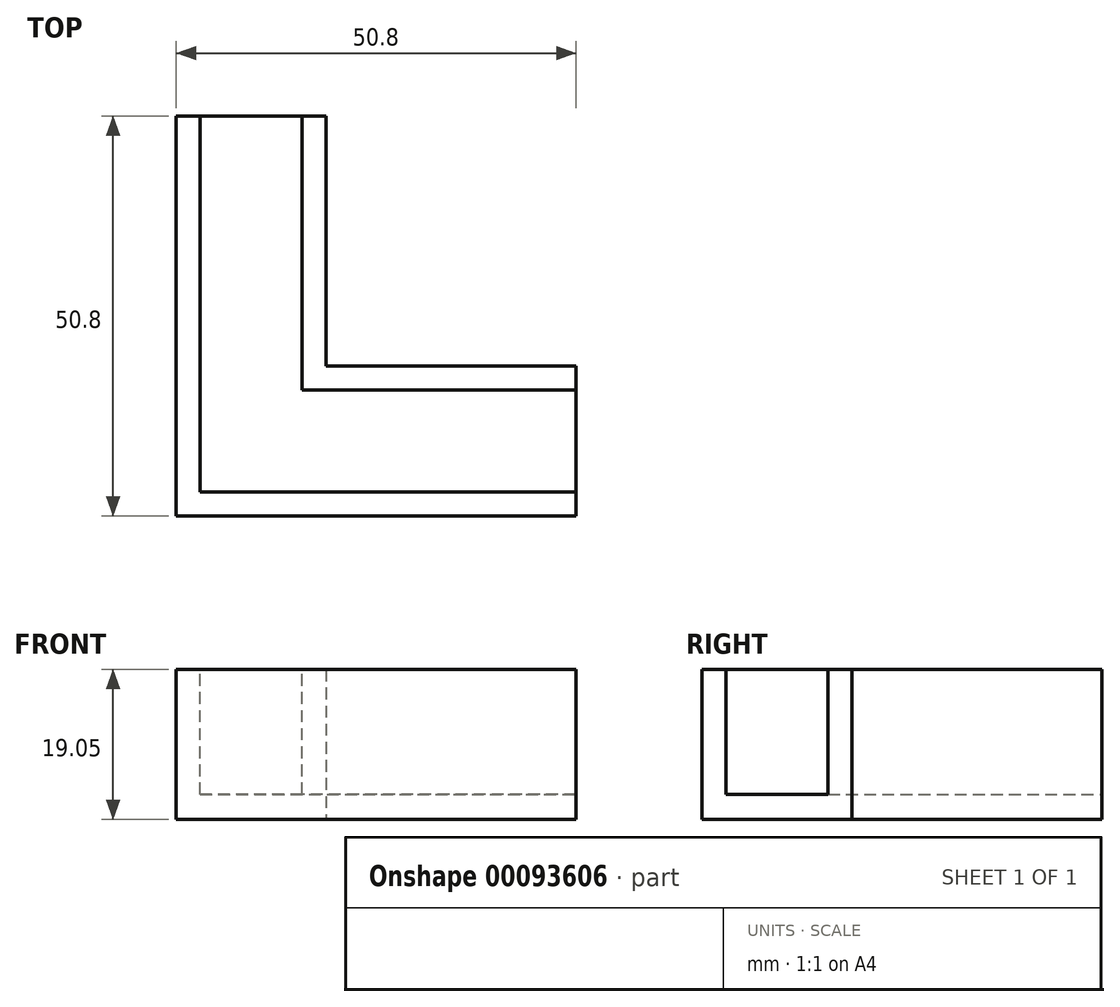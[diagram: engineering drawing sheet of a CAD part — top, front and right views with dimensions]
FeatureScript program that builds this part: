
annotation { "Feature Type Name" : "Feature", "Feature Type Description" : "" }
export const myFeature = defineFeature(function(context is Context, id is Id, definition is map)
    precondition{}
    {
        {
            var Q0;
            Q0=qCreatedBy(makeId("Top.planeOp"),FACE);
            var sketch = newSketch(context, id + "F0", { "sketchPlane" : qUnion([Q0])});
            skLineSegment(sketch, "E0", {"start": v(0, 0) * mm, "end": v(50.8, 0) * mm});
            skLineSegment(sketch, "E1", {"start": v(50.8, 0) * mm, "end": v(50.8, 19.05) * mm});
            skLineSegment(sketch, "E2", {"start": v(50.8, 19.05) * mm, "end": v(19.05, 19.05) * mm});
            skLineSegment(sketch, "E3", {"start": v(19.05, 19.05) * mm, "end": v(19.05, 50.8) * mm});
            skLineSegment(sketch, "E4", {"start": v(19.05, 50.8) * mm, "end": v(0, 50.8) * mm});
            skLineSegment(sketch, "E5", {"start": v(0, 50.8) * mm, "end": v(0, 0) * mm});
            skSolve(sketch);
        }
        {
            var Q0;
            Q0 = qSketchRegion(id + "F0", true);
            extrude(context, id + "F1", {"entities" : qUnion([Q0]), "depth" : 19.05 * mm});
        }
        {
            var Q0;
            Q0=makeQuery(id+"F1.opExtrude","CAP_FACE",FACE,{"disambiguationData":[OSD([sQuery(id+"F0.wireOp",EDGE,"E0"),sQuery(id+"F0.wireOp",EDGE,"E1"),sQuery(id+"F0.wireOp",EDGE,"E2"),sQuery(id+"F0.wireOp",EDGE,"E3"),sQuery(id+"F0.wireOp",EDGE,"E4"),sQuery(id+"F0.wireOp",EDGE,"E5")])],"isStart":false});
            var sketch = newSketch(context, id + "F2", { "sketchPlane" : qUnion([Q0])});
            skLineSegment(sketch, "E6.0", {"start": v(9.86, 41.61) * mm, "end": v(9.19, 41.61) * mm});
            skLineSegment(sketch, "E7.0", {"start": v(16, 16) * mm, "end": v(16, 50.8) * mm});
            skLineSegment(sketch, "E7.1", {"start": v(50.8, 16) * mm, "end": v(16, 16) * mm});
            skLineSegment(sketch, "E8.0", {"start": v(3.05, 3.05) * mm, "end": v(50.8, 3.05) * mm});
            skLineSegment(sketch, "E8.1", {"start": v(3.05, 50.8) * mm, "end": v(3.05, 3.05) * mm});
            skLineSegment(sketch, "E9", {"start": v(3.05, 50.8) * mm, "end": v(16, 50.8) * mm});
            skLineSegment(sketch, "E10", {"start": v(50.8, 16) * mm, "end": v(50.8, 3.05) * mm});
            skSolve(sketch);
        }
        {
            var Q0;
            Q0 = qSketchRegion(id + "F2", true);
            extrude(context, id + "F3", {"entities" : qUnion([Q0]), "operationType" : NewBodyOperationType.REMOVE, "oppositeDirection" : true, "depth" : 15.88 * mm});
        }
    });
